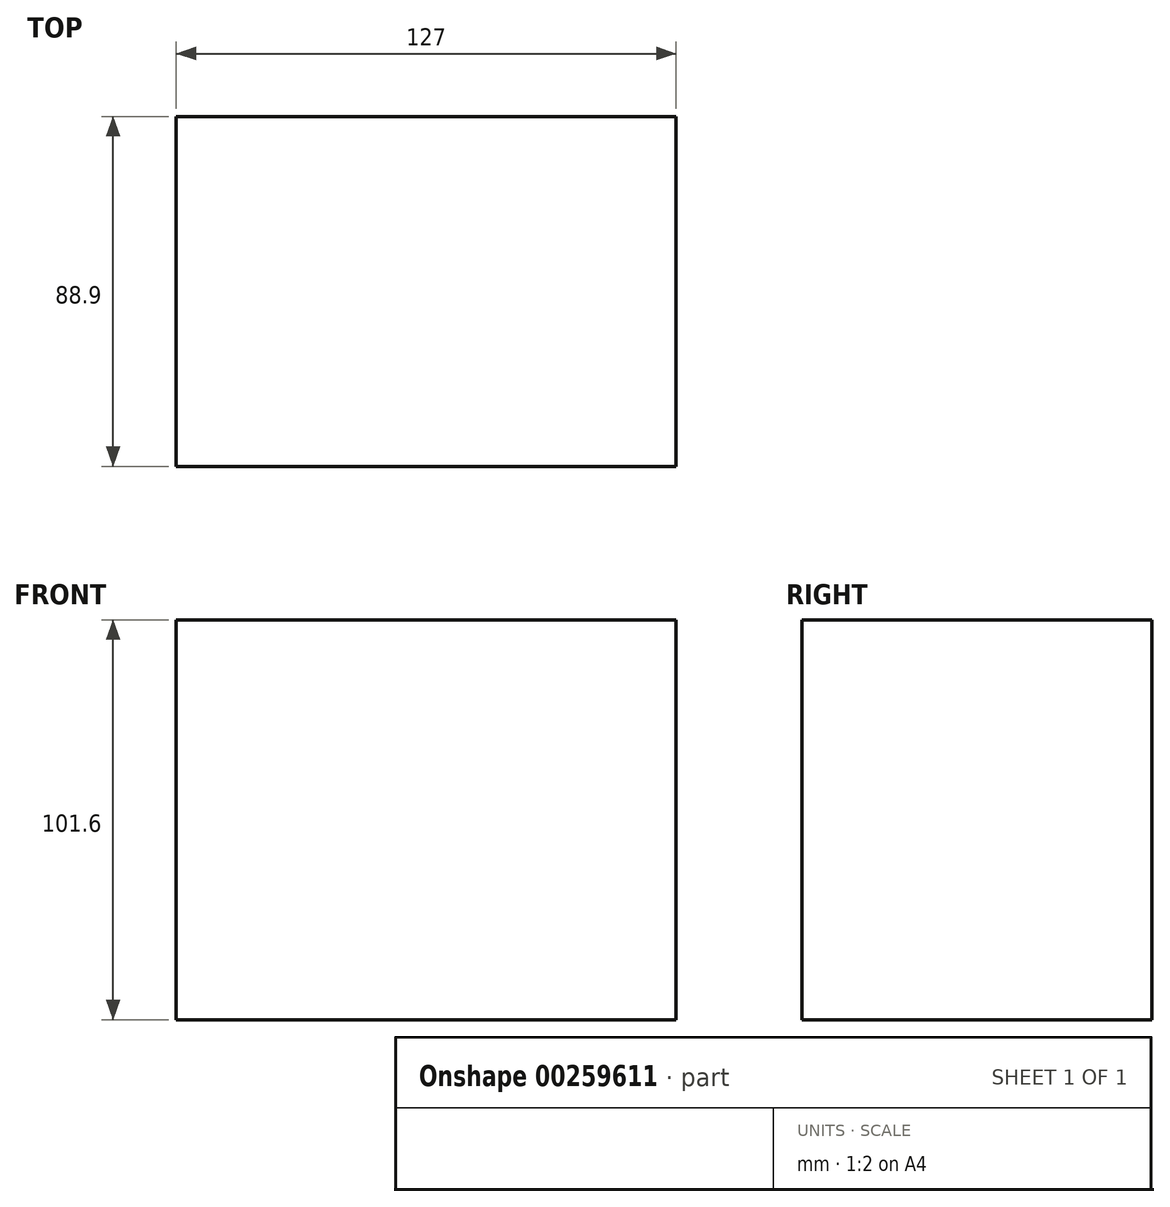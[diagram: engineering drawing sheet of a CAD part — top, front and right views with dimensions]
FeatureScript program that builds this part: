
annotation { "Feature Type Name" : "Feature", "Feature Type Description" : "" }
export const myFeature = defineFeature(function(context is Context, id is Id, definition is map)
    precondition{}
    {
        {
            var Q0;
            Q0=qCreatedBy(makeId("Top.planeOp"),FACE);
            var sketch = newSketch(context, id + "F0", { "sketchPlane" : qUnion([Q0])});
            skLineSegment(sketch, "E0.bottom", {"start": v(63.5, -44.45) * mm, "end": v(-63.5, -44.45) * mm});
            skLineSegment(sketch, "E0.top", {"start": v(63.5, 44.45) * mm, "end": v(-63.5, 44.45) * mm});
            skLineSegment(sketch, "E0.left", {"start": v(63.5, -44.45) * mm, "end": v(63.5, 44.45) * mm});
            skLineSegment(sketch, "E0.right", {"start": v(-63.5, -44.45) * mm, "end": v(-63.5, 44.45) * mm});
            skPoint(sketch, "E0.middle", {"position": v(0, 0) * mm});
            skSolve(sketch);
        }
        {
            var Q0;
            Q0=makeQuery(id+"F0.imprint","IMPRINT",FACE,{"disambiguationData":[TD([[makeQuery(id+"F0.imprint","IMPRINT",EDGE,{"derivedFrom":sQuery(id+"F0.wireOp",EDGE,"E0.bottom")}),-1.0]])]});
            extrude(context, id + "F1", {"entities" : qUnion([Q0]), "depth" : 101.6 * mm});
        }
    });
